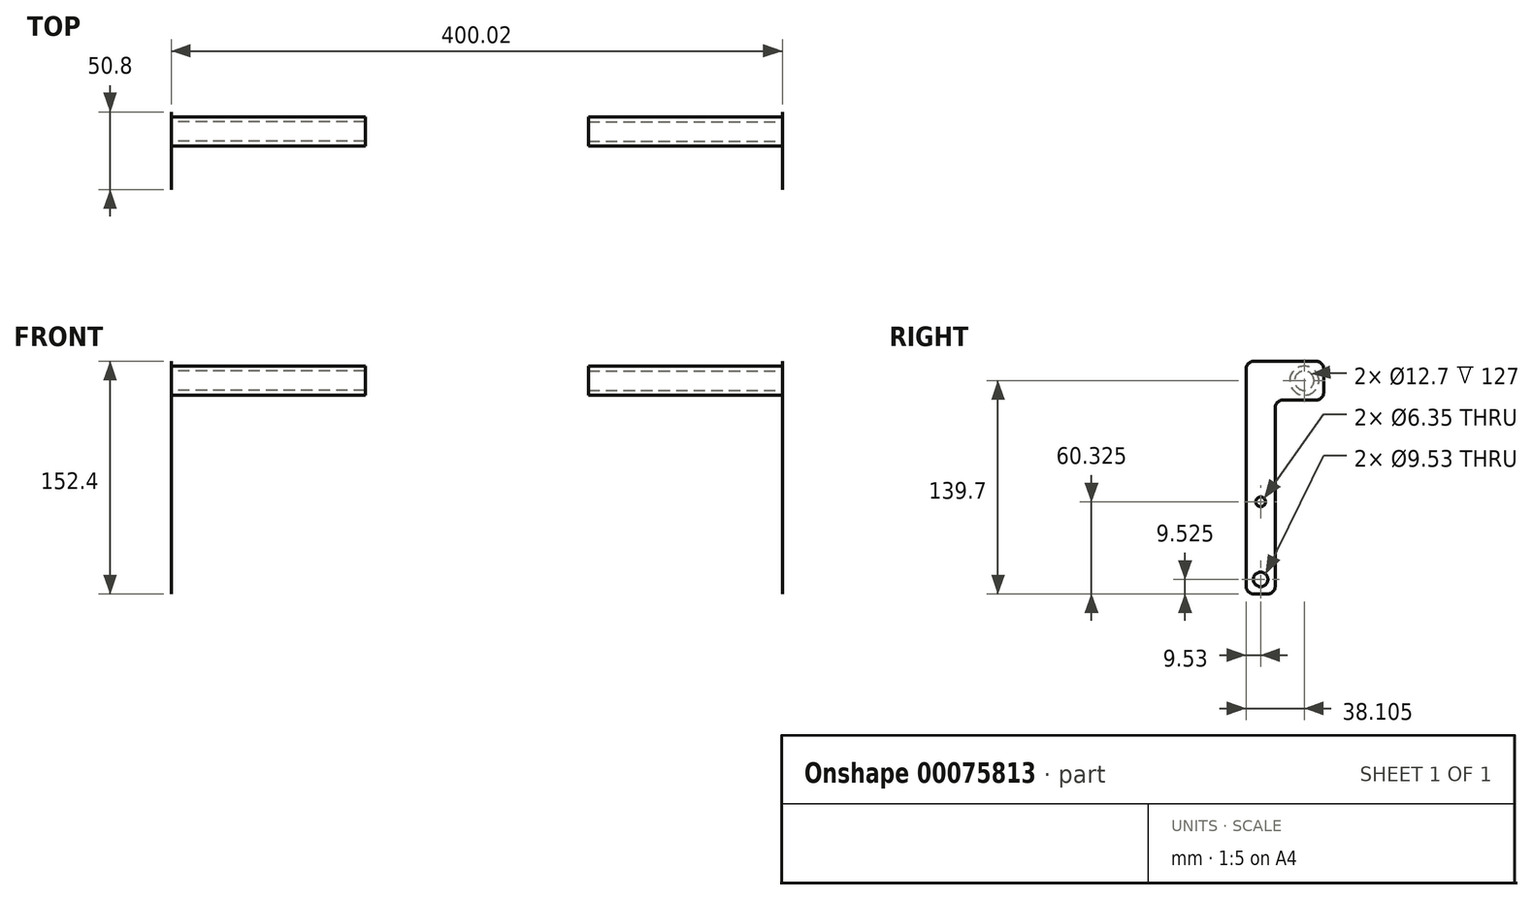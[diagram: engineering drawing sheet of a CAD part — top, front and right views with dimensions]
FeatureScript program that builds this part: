
annotation { "Feature Type Name" : "Feature", "Feature Type Description" : "" }
export const myFeature = defineFeature(function(context is Context, id is Id, definition is map)
    precondition{}
    {
        {
            var Q0;
            Q0=qCreatedBy(makeId("Right.planeOp"),FACE);
            var sketch = newSketch(context, id + "F0", { "sketchPlane" : qUnion([Q0])});
            skLineSegment(sketch, "E0.bottom", {"start": v(-9.52, 0) * mm, "end": v(9.52, 0) * mm});
            skLineSegment(sketch, "E0.top", {"start": v(-9.53, 152.4) * mm, "end": v(9.53, 152.4) * mm});
            skLineSegment(sketch, "E0.left", {"start": v(-9.52, 0) * mm, "end": v(-9.53, 152.4) * mm});
            skLineSegment(sketch, "E0.right", {"start": v(9.53, 0) * mm, "end": v(9.52, 152.4) * mm});
            skLineSegment(sketch, "E1.bottom", {"start": v(9.53, 152.4) * mm, "end": v(41.27, 152.4) * mm});
            skLineSegment(sketch, "E1.top", {"start": v(9.52, 127) * mm, "end": v(41.27, 127) * mm});
            skLineSegment(sketch, "E1.left", {"start": v(9.53, 152.4) * mm, "end": v(9.53, 127) * mm});
            skLineSegment(sketch, "E1.right", {"start": v(41.27, 152.4) * mm, "end": v(41.27, 127) * mm});
            skSolve(sketch);
        }
        {
            var Q0;
            Q0 = qSketchRegion(id + "F0", true);
            extrude(context, id + "F1", {"entities" : qUnion([Q0]), "oppositeDirection" : true, "depth" : 1 / 101.6 * mm});
        }
        {
            var Q0;
            Q0=makeQuery(id+"F1.opExtrude","CAP_FACE",FACE,{"disambiguationData":[OSD([sQuery(id+"F0.wireOp",EDGE,"E0.bottom"),sQuery(id+"F0.wireOp",EDGE,"E0.top"),sQuery(id+"F0.wireOp",EDGE,"E0.left"),sQuery(id+"F0.wireOp",EDGE,"E0.right"),sQuery(id+"F0.wireOp",EDGE,"E1.bottom"),sQuery(id+"F0.wireOp",EDGE,"E1.top"),sQuery(id+"F0.wireOp",EDGE,"E1.right")])],"isStart":true});
            var sketch = newSketch(context, id + "F2", { "sketchPlane" : qUnion([Q0])});
            skCircle(sketch, "E2", {"center": v(28.57, 139.7) * mm, "radius": 9.53 * mm});
            skPoint(sketch, "E2.centerSnap0", {"position": v(41.27, 139.7) * mm});
            skCircle(sketch, "E3", {"center": v(28.57, 139.7) * mm, "radius": 6.35 * mm});
            skSolve(sketch);
        }
        {
            var Q0;
            Q0 = qSketchRegion(id + "F2", true);
            extrude(context, id + "F3", {"entities" : qUnion([Q0]), "operationType" : NewBodyOperationType.ADD, "depth" : 127 * mm});
        }
        {
            var Q0;
            Q0=makeQuery(id+"F1.opExtrude","SWEPT_EDGE",EDGE,{"disambiguationData":[OSD([sQuery(id+"F0.wireOp",EDGE,"E0.top"),sQuery(id+"F0.wireOp",EDGE,"E0.left")])]});
            var Q1;
            Q1=makeQuery(id+"F1.opExtrude","SWEPT_EDGE",EDGE,{"disambiguationData":[OSD([sQuery(id+"F0.wireOp",EDGE,"E0.right"),sQuery(id+"F0.wireOp",EDGE,"E1.top"),sQuery(id+"F0.wireOp",EDGE,"E1.left")])]});
            var Q2;
            Q2=makeQuery(id+"F1.opExtrude","SWEPT_EDGE",EDGE,{"disambiguationData":[OSD([sQuery(id+"F0.wireOp",EDGE,"E1.top"),sQuery(id+"F0.wireOp",EDGE,"E1.right")])]});
            var Q3;
            Q3=makeQuery(id+"F1.opExtrude","SWEPT_EDGE",EDGE,{"disambiguationData":[OSD([sQuery(id+"F0.wireOp",EDGE,"E1.bottom"),sQuery(id+"F0.wireOp",EDGE,"E1.right")])]});
            var Q4;
            Q4=makeQuery(id+"F1.opExtrude","SWEPT_EDGE",EDGE,{"disambiguationData":[OSD([sQuery(id+"F0.wireOp",EDGE,"E0.bottom"),sQuery(id+"F0.wireOp",EDGE,"E0.right")])]});
            var Q5;
            Q5=makeQuery(id+"F1.opExtrude","SWEPT_EDGE",EDGE,{"disambiguationData":[OSD([sQuery(id+"F0.wireOp",EDGE,"E0.bottom"),sQuery(id+"F0.wireOp",EDGE,"E0.left")])]});
            fillet(context, id + "F4", {"entities" : qUnion([Q0, Q1, Q2, Q3, Q4, Q5]), "radius" : 5 * mm, "tangentPropagation" : true, "allowEdgeOverflow" : false});
        }
        {
            var Q0;
            Q0=makeQuery(id+"F1.opExtrude","CAP_FACE",FACE,{"disambiguationData":[OSD([sQuery(id+"F0.wireOp",EDGE,"E0.bottom"),sQuery(id+"F0.wireOp",EDGE,"E0.top"),sQuery(id+"F0.wireOp",EDGE,"E0.left"),sQuery(id+"F0.wireOp",EDGE,"E0.right"),sQuery(id+"F0.wireOp",EDGE,"E1.bottom"),sQuery(id+"F0.wireOp",EDGE,"E1.top"),sQuery(id+"F0.wireOp",EDGE,"E1.right")])],"isStart":true});
            var sketch = newSketch(context, id + "F5", { "sketchPlane" : qUnion([Q0])});
            skCircle(sketch, "E4", {"center": v(0, 9.53) * mm, "radius": 4.76 * mm});
            skCircle(sketch, "E5", {"center": v(0, 60.33) * mm, "radius": 3.18 * mm});
            skSolve(sketch);
        }
        {
            var Q0;
            Q0 = qSketchRegion(id + "F5", true);
            extrude(context, id + "F6", {"entities" : qUnion([Q0]), "operationType" : NewBodyOperationType.REMOVE, "endBound" : BoundingType.THROUGH_ALL, "oppositeDirection" : true, "depth" : 25 * mm});
        }
        {
            var Q0;
            Q0=qCreatedBy(makeId("Right.planeOp"),FACE);
            cPlane(context, id + "F7", {"entities" : qUnion([Q0]), "cplaneType" : CPlaneType.OFFSET, "offset" : 200 * mm, "width" : 150 * mm, "height" : 150 * mm});
        }
        {
            var Q0;
            Q0=makeQuery(id+"F1.opExtrude","SWEPT_BODY",BODY,{"disambiguationData":[OSD([sQuery(id+"F0.wireOp",EDGE,"E0.bottom"),sQuery(id+"F0.wireOp",EDGE,"E0.top"),sQuery(id+"F0.wireOp",EDGE,"E0.left"),sQuery(id+"F0.wireOp",EDGE,"E0.right"),sQuery(id+"F0.wireOp",EDGE,"E1.bottom"),sQuery(id+"F0.wireOp",EDGE,"E1.top"),sQuery(id+"F0.wireOp",EDGE,"E1.right")])]});
            var Q1;
            Q1=qCreatedBy(id+"F7.planeOp",FACE);
            mirror(context, id + "F8", {"entities" : qUnion([Q0]), "mirrorPlane" : qUnion([Q1])});
        }
    });
